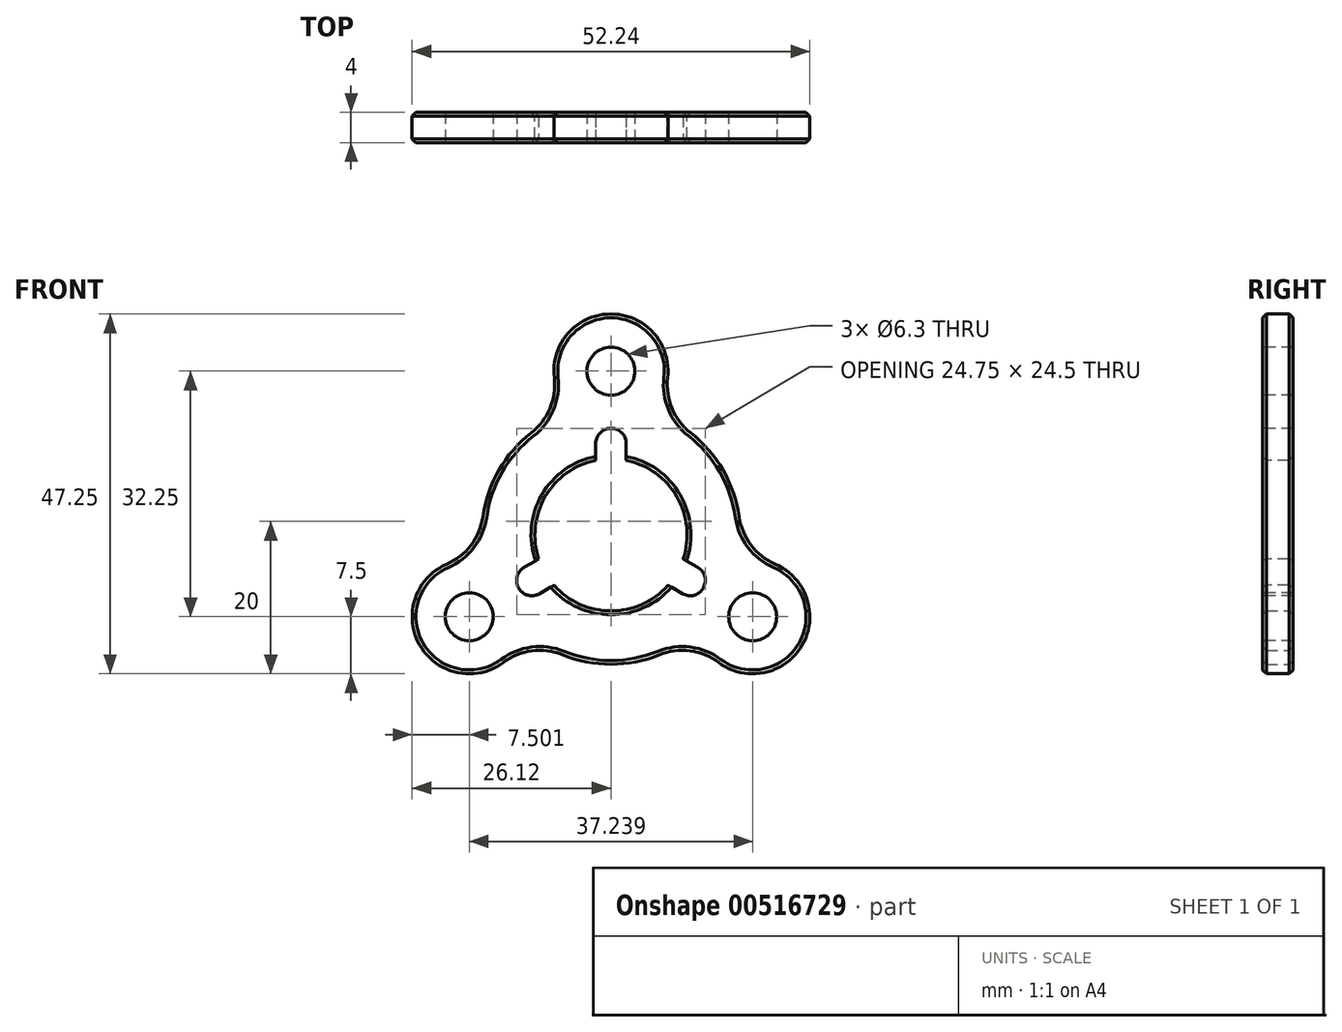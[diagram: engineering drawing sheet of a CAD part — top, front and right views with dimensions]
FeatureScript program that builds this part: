
annotation { "Feature Type Name" : "Feature", "Feature Type Description" : "" }
export const myFeature = defineFeature(function(context is Context, id is Id, definition is map)
    precondition{}
    {
        {
            var Q0;
            Q0=qCreatedBy(makeId("Front.planeOp"),FACE);
            var sketch = newSketch(context, id + "F0", { "sketchPlane" : qUnion([Q0])});
            skCircle(sketch, "E0", {"center": v(0, 0) * mm, "radius": 10 * mm});
            skArc(sketch, "E1", {"start": v(-25.11, 14.5) * mm, "mid": v(-29, 0) * mm, "end": v(-25.11, -14.5) * mm});
            skLineSegment(sketch, "E2", {"start": v(0, 0) * mm, "end": v(0, -29) * mm, "construction": true});
            skLineSegment(sketch, "E3", {"start": v(-25.11, 14.5) * mm, "end": v(0, 0) * mm, "construction": true});
            skLineSegment(sketch, "E4", {"start": v(25.11, 14.5) * mm, "end": v(0, 0) * mm, "construction": true});
            skLineSegment(sketch, "E5.MirrorCS", {"start": v(-25.11, -14.5) * mm, "end": v(0, 0) * mm, "construction": true});
            skLineSegment(sketch, "E6.MirrorCS", {"start": v(25.11, -14.5) * mm, "end": v(0, 0) * mm, "construction": true});
            skCircle(sketch, "E7", {"center": v(0, 0) * mm, "radius": 21.5 * mm, "construction": true});
            skArc(sketch, "E8", {"start": v(7.45, 20.63) * mm, "mid": v(0, 29) * mm, "end": v(-7.45, 20.63) * mm});
            skArc(sketch, "E9", {"start": v(14.14, -16.77) * mm, "mid": v(25.11, -14.5) * mm, "end": v(21.59, -3.86) * mm});
            skArc(sketch, "E10", {"start": v(-21.59, -3.86) * mm, "mid": v(-25.11, -14.5) * mm, "end": v(-14.14, -16.77) * mm});
            skArc(sketch, "E11", {"start": v(-10.47, 13.4) * mm, "mid": v(-14.72, 8.5) * mm, "end": v(-16.83, 2.37) * mm});
            skArc(sketch, "E12.trimOffspring", {"start": v(0, -29) * mm, "mid": v(14.5, -25.11) * mm, "end": v(25.11, -14.5) * mm});
            skArc(sketch, "E13.trimOffspring", {"start": v(-6.37, -15.76) * mm, "mid": v(0, -17) * mm, "end": v(6.37, -15.76) * mm});
            skArc(sketch, "E14.trimOffspring", {"start": v(16.83, 2.37) * mm, "mid": v(14.72, 8.5) * mm, "end": v(10.47, 13.4) * mm});
            skArc(sketch, "E15.trimOffspring", {"start": v(25.11, 14.5) * mm, "mid": v(14.5, 25.11) * mm, "end": v(0, 29) * mm});
            skPoint(sketch, "E16.visualSharp", {"position": v(-5.27, 16.16) * mm});
            skArc(sketch, "E16.filletArc", {"start": v(-10.47, 13.4) * mm, "mid": v(-8.01, 16.62) * mm, "end": v(-7.45, 20.63) * mm});
            skPoint(sketch, "E17.visualSharp", {"position": v(-16.63, -3.52) * mm});
            skArc(sketch, "E17.filletArc", {"start": v(-21.59, -3.86) * mm, "mid": v(-18.4, -1.37) * mm, "end": v(-16.83, 2.37) * mm});
            skPoint(sketch, "E18.visualSharp", {"position": v(-11.36, -12.64) * mm});
            skArc(sketch, "E18.filletArc", {"start": v(-6.37, -15.76) * mm, "mid": v(-10.38, -15.25) * mm, "end": v(-14.14, -16.77) * mm});
            skPoint(sketch, "E19.visualSharp", {"position": v(11.36, -12.64) * mm});
            skArc(sketch, "E19.filletArc", {"start": v(14.14, -16.77) * mm, "mid": v(10.38, -15.25) * mm, "end": v(6.37, -15.76) * mm});
            skPoint(sketch, "E20.visualSharp", {"position": v(16.63, -3.52) * mm});
            skArc(sketch, "E20.filletArc", {"start": v(16.83, 2.37) * mm, "mid": v(18.4, -1.37) * mm, "end": v(21.59, -3.86) * mm});
            skPoint(sketch, "E21.visualSharp", {"position": v(5.27, 16.16) * mm});
            skArc(sketch, "E21.filletArc", {"start": v(7.45, 20.63) * mm, "mid": v(8.01, 16.62) * mm, "end": v(10.47, 13.4) * mm});
            skSolve(sketch);
        }
        {
            var Q0;
            Q0=qSketchRegion(id+"F0",true);
            extrude(context, id + "F1", {"entities" : qUnion([Q0]), "depth" : 2 * mm, "offsetDistance" : 25 * mm, "hasSecondDirection" : true, "secondDirectionOppositeDirection" : true, "secondDirectionDepth" : 2 * mm});
        }
        {
            var Q0;
            Q0=makeQuery(id+"F1.opExtrude","CAP_FACE",FACE,{"disambiguationData":[OSD([sQuery(id+"F0.wireOp",EDGE,"E0"),sQuery(id+"F0.wireOp",EDGE,"E1")])],"isStart":false});
            var sketch = newSketch(context, id + "F2", { "sketchPlane" : qUnion([Q0])});
            skLineSegment(sketch, "E22", {"start": v(0, 0) * mm, "end": v(0, 29) * mm, "construction": true});
            skLineSegment(sketch, "E23", {"start": v(0, 0) * mm, "end": v(-25.11, -14.5) * mm, "construction": true});
            skLineSegment(sketch, "E24", {"start": v(0, 0) * mm, "end": v(25.11, -14.5) * mm, "construction": true});
            skPoint(sketch, "E25", {"position": v(0, 21.5) * mm});
            skPoint(sketch, "E26", {"position": v(-18.62, -10.75) * mm});
            skPoint(sketch, "E27", {"position": v(18.62, -10.75) * mm});
            skCircle(sketch, "E28", {"center": v(0, 0) * mm, "radius": 21.5 * mm, "construction": true});
            skSolve(sketch);
        }
        {
            var Q0;
            Q0=sQuery(id+"F2.wireOp",VERTEX,"E25");
            var Q1;
            Q1=sQuery(id+"F2.wireOp",VERTEX,"E26");
            var Q2;
            Q2=sQuery(id+"F2.wireOp",VERTEX,"E27");
            var Q3;
            Q3=makeQuery(id+"F1.opExtrude","SWEPT_BODY",BODY,{"disambiguationData":[OSD([sQuery(id+"F0.wireOp",EDGE,"E0"),sQuery(id+"F0.wireOp",EDGE,"E1")])]});
            hole(context, id + "F3", {"style" : HoleStyle.SIMPLE, "endStyle" : HoleEndStyle.THROUGH, "standardTappedOrClearance" : lookupTablePath({ "standard" : "ISO", "fit" : "Close", "size" : "M6", "type" : "Clearance" }), "standardBlindInLast" : lookupTablePath({ "fit" : "Close", "standard" : "ISO", "size" : "M6", "type" : "Clearance" }), "holeDiameter" : 6.3 * mm, "isTappedThrough" : true, "tappedDepth" : 12 * mm, "tapClearance" : 3, "locations" : qUnion([Q0, Q1, Q2]), "scope" : qUnion([Q3])});
        }
        {
            var Q0;
            Q0=makeQuery(id+"F1.opExtrude","CAP_EDGE",EDGE,{"disambiguationData":[OSD([sQuery(id+"F0.wireOp",EDGE,"E0")])],"isStart":false});
            var Q1;
            Q1=makeQuery(id+"F1.opExtrude","CAP_EDGE",EDGE,{"disambiguationData":[OSD([sQuery(id+"F0.wireOp",EDGE,"E0")])],"isStart":true});
            var Q2;
            Q2=makeQuery(id+"F1.opExtrude","CAP_EDGE",EDGE,{"disambiguationData":[OSD([sQuery(id+"F0.wireOp",EDGE,"E8")])],"isStart":false});
            var Q3;
            Q3=makeQuery(id+"F1.opExtrude","CAP_EDGE",EDGE,{"disambiguationData":[OSD([sQuery(id+"F0.wireOp",EDGE,"E8")])],"isStart":true});
            chamfer(context, id + "F4", {"entities" : qUnion([Q0, Q1, Q2, Q3]), "width" : .5 * mm, "tangentPropagation" : true});
        }
        {
            var Q0;
            Q0=makeQuery(id+"F1.opExtrude","CAP_FACE",FACE,{"disambiguationData":[OSD([sQuery(id+"F0.wireOp",EDGE,"E0"),sQuery(id+"F0.wireOp",EDGE,"E8"),sQuery(id+"F0.wireOp",EDGE,"E9"),sQuery(id+"F0.wireOp",EDGE,"E10"),sQuery(id+"F0.wireOp",EDGE,"E11"),sQuery(id+"F0.wireOp",EDGE,"E13.trimOffspring"),sQuery(id+"F0.wireOp",EDGE,"E14.trimOffspring"),sQuery(id+"F0.wireOp",EDGE,"E16.filletArc"),sQuery(id+"F0.wireOp",EDGE,"E17.filletArc"),sQuery(id+"F0.wireOp",EDGE,"E18.filletArc"),sQuery(id+"F0.wireOp",EDGE,"E19.filletArc"),sQuery(id+"F0.wireOp",EDGE,"E20.filletArc"),sQuery(id+"F0.wireOp",EDGE,"E21.filletArc")])],"isStart":false});
            var sketch = newSketch(context, id + "F5", { "sketchPlane" : qUnion([Q0])});
            skArc(sketch, "E29.0", {"start": v(2, 9.8) * mm, "mid": v(0, 10) * mm, "end": v(-2, 9.8) * mm});
            skLineSegment(sketch, "E30", {"start": v(-2, 9.8) * mm, "end": v(-2, 12) * mm});
            skLineSegment(sketch, "E31", {"start": v(2, 9.8) * mm, "end": v(2, 12) * mm});
            skArc(sketch, "E32", {"start": v(2, 12) * mm, "mid": v(0, 14) * mm, "end": v(-2, 12) * mm});
            skArc(sketch, "E33.1.0", {"start": v(-11.4, -4.27) * mm, "mid": v(-12.12, -7) * mm, "end": v(-9.4, -7.73) * mm});
            skLineSegment(sketch, "E33.1.1", {"start": v(-7.49, -6.63) * mm, "end": v(-9.4, -7.73) * mm});
            skArc(sketch, "E33.1.2", {"start": v(-9.49, -3.17) * mm, "mid": v(-8.66, -5) * mm, "end": v(-7.49, -6.63) * mm});
            skLineSegment(sketch, "E33.1.3", {"start": v(-9.49, -3.17) * mm, "end": v(-11.4, -4.27) * mm});
            skArc(sketch, "E33.2.0", {"start": v(9.4, -7.73) * mm, "mid": v(12.12, -7) * mm, "end": v(11.4, -4.27) * mm});
            skLineSegment(sketch, "E33.2.1", {"start": v(9.49, -3.17) * mm, "end": v(11.4, -4.27) * mm});
            skArc(sketch, "E33.2.2", {"start": v(7.49, -6.63) * mm, "mid": v(8.66, -5) * mm, "end": v(9.49, -3.17) * mm});
            skLineSegment(sketch, "E33.2.3", {"start": v(7.49, -6.63) * mm, "end": v(9.4, -7.73) * mm});
            skLineSegment(sketch, "E34", {"start": v(0, 0) * mm, "end": v(-10.4, -6) * mm, "construction": true});
            skLineSegment(sketch, "E35", {"start": v(0, 0) * mm, "end": v(10.4, -6) * mm, "construction": true});
            skLineSegment(sketch, "E36", {"start": v(0, 0) * mm, "end": v(0, 12) * mm, "construction": true});
            skSolve(sketch);
        }
        {
            var Q0;
            Q0 = qSketchRegion(id + "F5", true);
            extrude(context, id + "F6", {"entities" : qUnion([Q0]), "operationType" : NewBodyOperationType.REMOVE, "endBound" : BoundingType.THROUGH_ALL, "oppositeDirection" : true, "depth" : 25 * mm, "offsetDistance" : 25 * mm});
        }
    });
